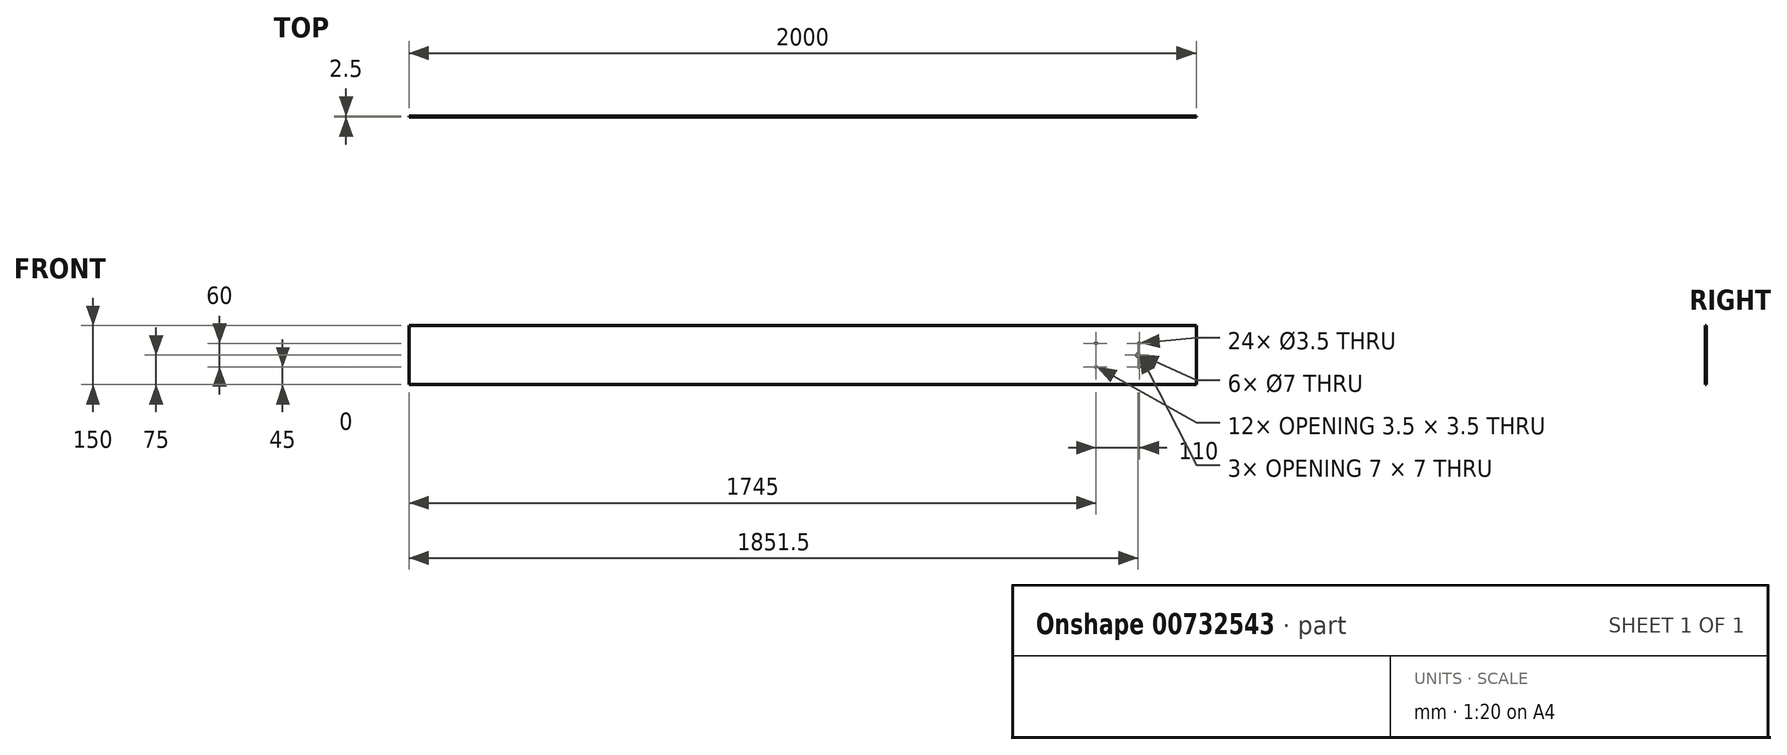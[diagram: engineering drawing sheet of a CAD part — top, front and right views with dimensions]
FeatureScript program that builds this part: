
annotation { "Feature Type Name" : "Feature", "Feature Type Description" : "" }
export const myFeature = defineFeature(function(context is Context, id is Id, definition is map)
    precondition{}
    {
        {
            var Q0;
            Q0=qCreatedBy(makeId("Front.planeOp"),FACE);
            var sketch = newSketch(context, id + "F0", { "sketchPlane" : qUnion([Q0])});
            skLineSegment(sketch, "E0.bottom", {"start": v(0, 0) * mm, "end": v(2000, 0) * mm});
            skLineSegment(sketch, "E0.top", {"start": v(0, 150) * mm, "end": v(2000, 150) * mm});
            skLineSegment(sketch, "E0.left", {"start": v(0, 0) * mm, "end": v(0, 150) * mm});
            skLineSegment(sketch, "E0.right", {"start": v(2000, 0) * mm, "end": v(2000, 150) * mm});
            skSolve(sketch);
        }
        {
            var Q0;
            Q0 = qSketchRegion(id + "F0", true);
            extrude(context, id + "F1", {"entities" : qUnion([Q0]), "depth" : 2.5 * mm, "offsetDistance" : 25 * mm});
        }
        {
            var Q0;
            Q0=makeQuery(id+"F1.opExtrude","CAP_FACE",FACE,{"disambiguationData":[OSD([sQuery(id+"F0.wireOp",EDGE,"E0.bottom"),sQuery(id+"F0.wireOp",EDGE,"E0.top"),sQuery(id+"F0.wireOp",EDGE,"E0.left"),sQuery(id+"F0.wireOp",EDGE,"E0.right")])],"isStart":true});
            var sketch = newSketch(context, id + "F2", { "sketchPlane" : qUnion([Q0])});
            skLineSegment(sketch, "E1", {"start": v(-1000, 150) * mm, "end": v(-1000, 0) * mm, "construction": true});
            skLineSegment(sketch, "E2", {"start": v(-1000, 75) * mm, "end": v(-1800, 75) * mm, "construction": true});
            skLineSegment(sketch, "E3.bottom", {"start": v(-1855, 105) * mm, "end": v(-1745, 105) * mm, "construction": true});
            skLineSegment(sketch, "E3.top", {"start": v(-1855, 45) * mm, "end": v(-1745, 45) * mm, "construction": true});
            skLineSegment(sketch, "E3.left", {"start": v(-1855, 105) * mm, "end": v(-1855, 45) * mm, "construction": true});
            skLineSegment(sketch, "E3.right", {"start": v(-1745, 105) * mm, "end": v(-1745, 45) * mm, "construction": true});
            skPoint(sketch, "E3.middle", {"position": v(-1800, 75) * mm});
            skCircle(sketch, "E4", {"center": v(-1855, 105) * mm, "radius": 1.75 * mm});
            skCircle(sketch, "E5", {"center": v(-1745, 105) * mm, "radius": 1.75 * mm});
            skCircle(sketch, "E6", {"center": v(-1745, 45) * mm, "radius": 1.75 * mm});
            skCircle(sketch, "E7", {"center": v(-1855, 45) * mm, "radius": 1.75 * mm});
            skCircle(sketch, "E8", {"center": v(-1851.5, 75) * mm, "radius": 3.5 * mm});
            skLineSegment(sketch, "E9", {"start": v(-1800, 75) * mm, "end": v(-1855, 75) * mm, "construction": true});
            skSolve(sketch);
        }
        {
            var Q0;
            Q0 = qSketchRegion(id + "F2", true);
            extrude(context, id + "F3", {"entities" : qUnion([Q0]), "operationType" : NewBodyOperationType.REMOVE, "endBound" : BoundingType.THROUGH_ALL, "oppositeDirection" : true, "depth" : 25 * mm, "offsetDistance" : 25 * mm});
        }
    });
